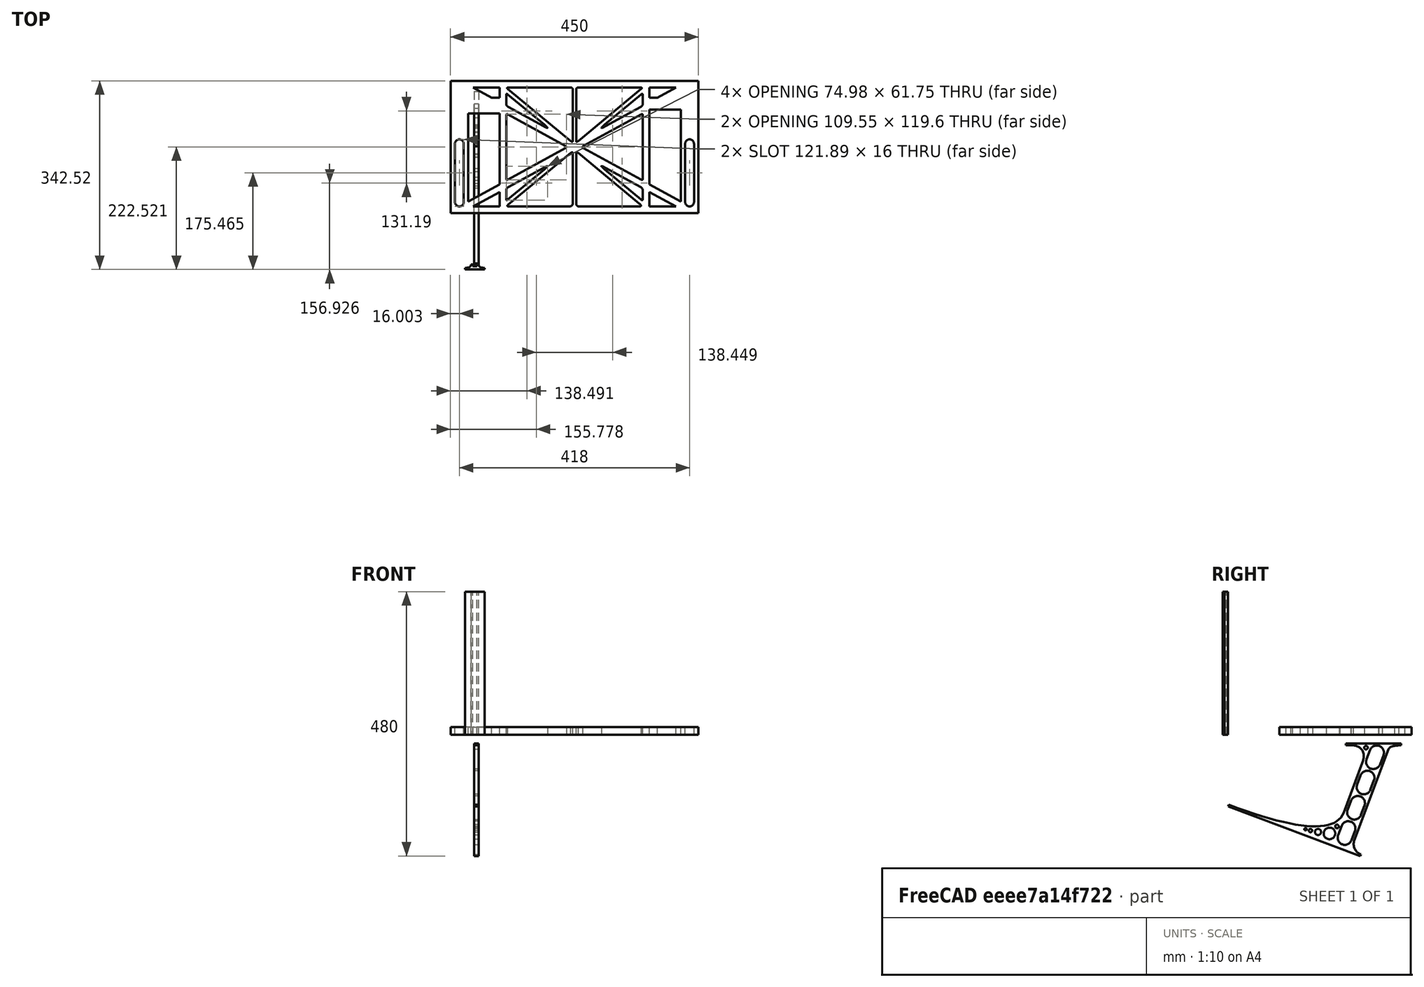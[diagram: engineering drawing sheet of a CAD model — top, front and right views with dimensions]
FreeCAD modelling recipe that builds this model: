
FCSTD DOCUMENT  (FreeCAD 0.19R0.19.2)
Label: laptopStand092
License: All rights reserved
LicenseURL: http://en.wikipedia.org/wiki/All_rights_reserved
objects: Sketcher::SketchObject×3, Part::Extrusion×3
note: 6 computed .brp shape members not serialized (recipe doc carries the construction recipe); baked Part::Feature solids carry a one-line shape summary decoded from their .brp

FEATURE [Sketcher::SketchObject] Sketch
  FullyConstrained = false
  sketch-geometry (251):
    g0: LineSegment StartX=-10.9272 StartY=-82.7794 StartZ=0 EndX=46.0728 EndY=-51.4823 EndZ=0
    g1: LineSegment StartX=366.073 StartY=-91.7794 StartZ=0 EndX=318.073 EndY=-65.424 EndZ=0
    g2: LineSegment StartX=-10.9272 StartY=77.3346 StartZ=0 EndX=-10.9272 EndY=-82.7794 EndZ=0
    g3: LineSegment StartX=375.073 StartY=-82.7794 StartZ=0 EndX=375.073 EndY=83.9235 EndZ=0
    g4: LineSegment StartX=-1.92719 StartY=-91.7794 StartZ=0 EndX=46.0728 EndY=-91.7794 EndZ=0
    g5: LineSegment StartX=318.073 StartY=124.221 StartZ=0 EndX=366.073 EndY=124.221 EndZ=0
    g6: LineSegment StartX=318.073 StartY=83.9235 StartZ=0 EndX=318.073 EndY=-51.4823 EndZ=0
    g7: LineSegment StartX=318.073 StartY=-51.4823 StartZ=0 EndX=375.073 EndY=-82.7794 EndZ=0
    g8: LineSegment StartX=318.073 StartY=-65.424 StartZ=0 EndX=318.073 EndY=-91.7794 EndZ=0
    g9: LineSegment StartX=318.073 StartY=-91.7794 StartZ=0 EndX=366.073 EndY=-91.7794 EndZ=0
    g10: LineSegment StartX=46.0728 StartY=-65.424 StartZ=0 EndX=-1.92719 EndY=-91.7794 EndZ=0
    g11: LineSegment StartX=46.0728 StartY=-65.424 StartZ=0 EndX=46.0728 EndY=-91.7794 EndZ=0
    g12: LineSegment StartX=46.0728 StartY=77.3346 StartZ=0 EndX=46.0728 EndY=-51.4823 EndZ=0
    g13: LineSegment StartX=-42.9272 StartY=136.221 StartZ=0 EndX=-42.9272 EndY=-103.779 EndZ=0
    g14: LineSegment StartX=407.073 StartY=136.221 StartZ=0 EndX=407.073 EndY=-103.779 EndZ=0
    g15: ArcOfCircle CenterX=-26.9272 CenterY=22.1087 CenterZ=0 NormalX=0 NormalY=0 NormalZ=1 AngleXU=0 Radius=8 StartAngle=1e-16 EndAngle=3.14159
    g16: ArcOfCircle CenterX=-26.9272 CenterY=-83.7794 CenterZ=0 NormalX=0 NormalY=0 NormalZ=1 AngleXU=0 Radius=8 StartAngle=3.14159 EndAngle=6.28319
    g17: LineSegment StartX=-34.9272 StartY=22.1087 StartZ=0 EndX=-34.9272 EndY=-83.7794 EndZ=0
    g18: LineSegment StartX=-18.9272 StartY=22.1087 StartZ=0 EndX=-18.9272 EndY=-83.7794 EndZ=0
    g19: ArcOfCircle CenterX=391.073 CenterY=22.1087 CenterZ=0 NormalX=0 NormalY=0 NormalZ=1 AngleXU=0 Radius=8 StartAngle=-4.4e-15 EndAngle=3.14159
    g20: LineSegment StartX=399.073 StartY=22.1087 StartZ=0 EndX=399.073 EndY=-83.7794 EndZ=0
    g21: LineSegment StartX=383.073 StartY=22.1087 StartZ=0 EndX=383.073 EndY=-83.7794 EndZ=0
    g22: ArcOfCircle CenterX=391.073 CenterY=-83.7794 CenterZ=0 NormalX=0 NormalY=0 NormalZ=1 AngleXU=0 Radius=8 StartAngle=3.14159 EndAngle=6.28319
    g23: Circle CenterX=175.022 CenterY=27.0628 CenterZ=0 NormalX=0 NormalY=0 NormalZ=1 AngleXU=0 Radius=1
    g24: Circle CenterX=179.022 CenterY=24.8665 CenterZ=0 NormalX=0 NormalY=0 NormalZ=1 AngleXU=0 Radius=1
    g25: Circle CenterX=179.022 CenterY=27.0628 CenterZ=0 NormalX=0 NormalY=0 NormalZ=1 AngleXU=0 Radius=1
    g26: BSplineCurve PolesCount=3 KnotsCount=2 Degree=2 IsPeriodic=0
    g27: GeomPoint X=175.022 Y=27.0628 Z=0
    g28: GeomPoint X=179.022 Y=27.0628 Z=0
    g29: Circle CenterX=189.124 CenterY=27.0628 CenterZ=0 NormalX=0 NormalY=0 NormalZ=1 AngleXU=0 Radius=1
    g30: Circle CenterX=185.124 CenterY=24.8665 CenterZ=0 NormalX=0 NormalY=0 NormalZ=1 AngleXU=0 Radius=1
    g31: Circle CenterX=185.124 CenterY=27.0628 CenterZ=0 NormalX=0 NormalY=0 NormalZ=1 AngleXU=0 Radius=1
    g32: BSplineCurve PolesCount=3 KnotsCount=2 Degree=2 IsPeriodic=0
    g33: GeomPoint X=189.124 Y=27.0628 Z=0
    g34: GeomPoint X=185.124 Y=27.0628 Z=0
    g35: Circle CenterX=175.022 CenterY=5.37834 CenterZ=0 NormalX=0 NormalY=0 NormalZ=1 AngleXU=0 Radius=1
    g36: Circle CenterX=179.022 CenterY=7.57463 CenterZ=0 NormalX=0 NormalY=0 NormalZ=1 AngleXU=0 Radius=1
    g37: Circle CenterX=179.022 CenterY=5.34704 CenterZ=0 NormalX=0 NormalY=0 NormalZ=1 AngleXU=0 Radius=1
    g38: BSplineCurve PolesCount=3 KnotsCount=2 Degree=2 IsPeriodic=0
    g39: GeomPoint X=175.022 Y=5.37834 Z=0
    g40: GeomPoint X=179.022 Y=5.34704 Z=0
    g41: Circle CenterX=189.124 CenterY=5.37834 CenterZ=0 NormalX=0 NormalY=0 NormalZ=1 AngleXU=0 Radius=1
    g42: Circle CenterX=185.124 CenterY=7.57463 CenterZ=0 NormalX=0 NormalY=0 NormalZ=1 AngleXU=0 Radius=1
    g43: Circle CenterX=185.124 CenterY=5.34704 CenterZ=0 NormalX=0 NormalY=0 NormalZ=1 AngleXU=0 Radius=1
    g44: BSplineCurve PolesCount=3 KnotsCount=2 Degree=2 IsPeriodic=0
    g45: GeomPoint X=189.124 Y=5.37834 Z=0
    g46: GeomPoint X=185.124 Y=5.34704 Z=0
    g47: Circle CenterX=165.871 CenterY=18.1458 CenterZ=0 NormalX=0 NormalY=0 NormalZ=1 AngleXU=0 Radius=1
    g48: Circle CenterX=169.377 CenterY=16.2206 CenterZ=0 NormalX=0 NormalY=0 NormalZ=1 AngleXU=0 Radius=1
    g49: Circle CenterX=165.871 CenterY=14.2954 CenterZ=0 NormalX=0 NormalY=0 NormalZ=1 AngleXU=0 Radius=1
    g50: BSplineCurve PolesCount=3 KnotsCount=2 Degree=2 IsPeriodic=0
    g51: GeomPoint X=165.871 Y=18.1458 Z=0
    g52: GeomPoint X=165.871 Y=14.2954 Z=0
    g53: Circle CenterX=198.275 CenterY=18.1458 CenterZ=0 NormalX=0 NormalY=0 NormalZ=1 AngleXU=0 Radius=1
    g54: Circle CenterX=194.768 CenterY=16.2206 CenterZ=0 NormalX=0 NormalY=0 NormalZ=1 AngleXU=0 Radius=1
    g55: Circle CenterX=198.275 CenterY=14.2954 CenterZ=0 NormalX=0 NormalY=0 NormalZ=1 AngleXU=0 Radius=1
    g56: BSplineCurve PolesCount=3 KnotsCount=2 Degree=2 IsPeriodic=0
    g57: GeomPoint X=198.275 Y=18.1458 Z=0
    g58: GeomPoint X=198.275 Y=14.2954 Z=0
    g59: LineSegment StartX=407.073 StartY=-103.779 StartZ=0 EndX=-42.9272 EndY=-103.779 EndZ=0
    g60: LineSegment StartX=407.073 StartY=136.221 StartZ=0 EndX=-42.9272 EndY=136.221 EndZ=0
    g61: LineSegment StartX=46.0728 StartY=77.3346 StartZ=0 EndX=-10.9272 EndY=77.3346 EndZ=0
    g62: LineSegment StartX=46.0728 StartY=105.865 StartZ=0 EndX=31.5028 EndY=105.865 EndZ=0
    g63: LineSegment StartX=46.0728 StartY=124.221 StartZ=0 EndX=46.0728 EndY=105.865 EndZ=0
    g64: LineSegment StartX=-1.92719 StartY=124.221 StartZ=0 EndX=31.5028 EndY=105.865 EndZ=0
    g65: LineSegment StartX=46.0728 StartY=124.221 StartZ=0 EndX=-1.92719 EndY=124.221 EndZ=0
    g66: LineSegment StartX=318.073 StartY=83.9235 StartZ=0 EndX=375.073 EndY=83.9235 EndZ=0
    g67: LineSegment StartX=318.073 StartY=105.865 StartZ=0 EndX=332.643 EndY=105.865 EndZ=0
    g68: LineSegment StartX=332.643 StartY=105.865 StartZ=0 EndX=366.073 EndY=124.221 EndZ=0
    g69: LineSegment StartX=318.073 StartY=124.221 StartZ=0 EndX=318.073 EndY=105.865 EndZ=0
    g70: Circle CenterX=125.607 CenterY=54.1951 CenterZ=0 NormalX=0 NormalY=0 NormalZ=1 AngleXU=0 Radius=1
    g71: Circle CenterX=139.632 CenterY=46.4944 CenterZ=0 NormalX=0 NormalY=0 NormalZ=1 AngleXU=0 Radius=1
    g72: Circle CenterX=127.326 CenterY=56.7187 CenterZ=0 NormalX=0 NormalY=0 NormalZ=1 AngleXU=0 Radius=1
    g73: BSplineCurve PolesCount=3 KnotsCount=2 Degree=2 IsPeriodic=0
    g74: GeomPoint X=125.607 Y=54.1951 Z=0
    g75: GeomPoint X=127.326 Y=56.7187 Z=0
    g76: Circle CenterX=236.821 CenterY=56.7187 CenterZ=0 NormalX=0 NormalY=0 NormalZ=1 AngleXU=0 Radius=1
    g77: Circle CenterX=224.513 CenterY=46.4944 CenterZ=0 NormalX=0 NormalY=0 NormalZ=1 AngleXU=0 Radius=1
    g78: Circle CenterX=238.538 CenterY=54.1951 CenterZ=0 NormalX=0 NormalY=0 NormalZ=1 AngleXU=0 Radius=1
    g79: BSplineCurve PolesCount=3 KnotsCount=2 Degree=2 IsPeriodic=0
    g80: GeomPoint X=236.821 Y=56.7187 Z=0
    g81: GeomPoint X=238.538 Y=54.1951 Z=0
    g82: Circle CenterX=238.538 CenterY=-21.7539 CenterZ=0 NormalX=0 NormalY=0 NormalZ=1 AngleXU=0 Radius=1
    g83: Circle CenterX=224.513 CenterY=-14.0532 CenterZ=0 NormalX=0 NormalY=0 NormalZ=1 AngleXU=0 Radius=1
    g84: Circle CenterX=236.821 CenterY=-24.2775 CenterZ=0 NormalX=0 NormalY=0 NormalZ=1 AngleXU=0 Radius=1
    g85: BSplineCurve PolesCount=3 KnotsCount=2 Degree=2 IsPeriodic=0
    g86: GeomPoint X=238.538 Y=-21.7539 Z=0
    g87: GeomPoint X=236.821 Y=-24.2775 Z=0
    g88: Circle CenterX=125.607 CenterY=-21.7539 CenterZ=0 NormalX=0 NormalY=0 NormalZ=1 AngleXU=0 Radius=1
    g89: Circle CenterX=139.632 CenterY=-14.0532 CenterZ=0 NormalX=0 NormalY=0 NormalZ=1 AngleXU=0 Radius=1
    g90: Circle CenterX=127.325 CenterY=-24.2775 CenterZ=0 NormalX=0 NormalY=0 NormalZ=1 AngleXU=0 Radius=1
    g91: BSplineCurve PolesCount=3 KnotsCount=2 Degree=2 IsPeriodic=0
    g92: GeomPoint X=125.607 Y=-21.7539 Z=0
    g93: GeomPoint X=127.325 Y=-24.2775 Z=0
    g94: Circle CenterX=302.996 CenterY=111.695 CenterZ=0 NormalX=0 NormalY=0 NormalZ=1 AngleXU=0 Radius=1
    g95: Circle CenterX=306.073 CenterY=114.251 CenterZ=0 NormalX=0 NormalY=0 NormalZ=1 AngleXU=0 Radius=1
    g96: Circle CenterX=306.073 CenterY=110.251 CenterZ=0 NormalX=0 NormalY=0 NormalZ=1 AngleXU=0 Radius=1
    g97: BSplineCurve PolesCount=3 KnotsCount=2 Degree=2 IsPeriodic=0
    g98: GeomPoint X=302.996 Y=111.695 Z=0
    g99: GeomPoint X=306.073 Y=110.251 Z=0
    g100: Circle CenterX=306.073 CenterY=95.2763 CenterZ=0 NormalX=0 NormalY=0 NormalZ=1 AngleXU=0 Radius=1
    g101: Circle CenterX=306.073 CenterY=91.2763 CenterZ=0 NormalX=0 NormalY=0 NormalZ=1 AngleXU=0 Radius=1
    g102: Circle CenterX=302.567 CenterY=89.3511 CenterZ=0 NormalX=0 NormalY=0 NormalZ=1 AngleXU=0 Radius=1
    g103: BSplineCurve PolesCount=3 KnotsCount=2 Degree=2 IsPeriodic=0
    g104: GeomPoint X=306.073 Y=95.2763 Z=0
    g105: GeomPoint X=302.567 Y=89.3511 Z=0
    g106: LineSegment StartX=306.073 StartY=110.251 StartZ=0 EndX=306.073 EndY=95.2763 EndZ=0
    g107: LineSegment StartX=302.996 StartY=111.695 StartZ=0 EndX=236.821 EndY=56.7187 EndZ=0
    g108: LineSegment StartX=238.538 StartY=54.1951 StartZ=0 EndX=302.567 EndY=89.3511 EndZ=0
    g109: Circle CenterX=61.1496 CenterY=111.695 CenterZ=0 NormalX=0 NormalY=0 NormalZ=1 AngleXU=0 Radius=1
    g110: Circle CenterX=58.0728 CenterY=114.251 CenterZ=0 NormalX=0 NormalY=0 NormalZ=1 AngleXU=0 Radius=1
    g111: Circle CenterX=58.0728 CenterY=110.251 CenterZ=0 NormalX=0 NormalY=0 NormalZ=1 AngleXU=0 Radius=1
    g112: BSplineCurve PolesCount=3 KnotsCount=2 Degree=2 IsPeriodic=0
    g113: GeomPoint X=61.1496 Y=111.695 Z=0
    g114: GeomPoint X=58.0728 Y=110.251 Z=0
    g115: Circle CenterX=61.5791 CenterY=89.3511 CenterZ=0 NormalX=0 NormalY=0 NormalZ=1 AngleXU=0 Radius=1
    g116: Circle CenterX=58.0728 CenterY=91.2763 CenterZ=0 NormalX=0 NormalY=0 NormalZ=1 AngleXU=0 Radius=1
    g117: Circle CenterX=58.0728 CenterY=95.2763 CenterZ=0 NormalX=0 NormalY=0 NormalZ=1 AngleXU=0 Radius=1
    g118: BSplineCurve PolesCount=3 KnotsCount=2 Degree=2 IsPeriodic=0
    g119: GeomPoint X=61.5791 Y=89.3511 Z=0
    g120: GeomPoint X=58.0728 Y=95.2763 Z=0
    g121: LineSegment StartX=58.0728 StartY=110.251 StartZ=0 EndX=58.0728 EndY=95.2763 EndZ=0
    g122: LineSegment StartX=61.1496 StartY=111.695 StartZ=0 EndX=127.326 EndY=56.7187 EndZ=0
    g123: LineSegment StartX=125.607 StartY=54.1951 StartZ=0 EndX=61.5791 EndY=89.3511 EndZ=0
    g124: Circle CenterX=61.5791 CenterY=-56.9099 CenterZ=0 NormalX=0 NormalY=0 NormalZ=1 AngleXU=0 Radius=1
    g125: Circle CenterX=58.0728 CenterY=-58.8351 CenterZ=0 NormalX=0 NormalY=0 NormalZ=1 AngleXU=0 Radius=1
    g126: Circle CenterX=58.0728 CenterY=-62.8351 CenterZ=0 NormalX=0 NormalY=0 NormalZ=1 AngleXU=0 Radius=1
    g127: BSplineCurve PolesCount=3 KnotsCount=2 Degree=2 IsPeriodic=0
    g128: GeomPoint X=61.5791 Y=-56.9099 Z=0
    g129: GeomPoint X=58.0728 Y=-62.8351 Z=0
    g130: Circle CenterX=58.0728 CenterY=-77.8102 CenterZ=0 NormalX=0 NormalY=0 NormalZ=1 AngleXU=0 Radius=1
    g131: Circle CenterX=58.0728 CenterY=-81.8102 CenterZ=0 NormalX=0 NormalY=0 NormalZ=1 AngleXU=0 Radius=1
    g132: Circle CenterX=61.1496 CenterY=-79.2541 CenterZ=0 NormalX=0 NormalY=0 NormalZ=1 AngleXU=0 Radius=1
    g133: BSplineCurve PolesCount=3 KnotsCount=2 Degree=2 IsPeriodic=0
    g134: GeomPoint X=58.0728 Y=-77.8102 Z=0
    g135: GeomPoint X=61.1496 Y=-79.2541 Z=0
    g136: LineSegment StartX=58.0728 StartY=-62.8351 StartZ=0 EndX=58.0728 EndY=-77.8102 EndZ=0
    g137: LineSegment StartX=61.1496 StartY=-79.2541 StartZ=0 EndX=127.325 EndY=-24.2775 EndZ=0
    g138: LineSegment StartX=125.607 StartY=-21.7539 StartZ=0 EndX=61.5791 EndY=-56.9099 EndZ=0
    g139: Circle CenterX=302.567 CenterY=-56.9099 CenterZ=0 NormalX=0 NormalY=0 NormalZ=1 AngleXU=0 Radius=1
    g140: Circle CenterX=306.073 CenterY=-58.8351 CenterZ=0 NormalX=0 NormalY=0 NormalZ=1 AngleXU=0 Radius=1
    g141: Circle CenterX=306.073 CenterY=-62.8351 CenterZ=0 NormalX=0 NormalY=0 NormalZ=1 AngleXU=0 Radius=1
    g142: BSplineCurve PolesCount=3 KnotsCount=2 Degree=2 IsPeriodic=0
    g143: GeomPoint X=302.567 Y=-56.9099 Z=0
    g144: GeomPoint X=306.073 Y=-62.8351 Z=0
    g145: Circle CenterX=302.996 CenterY=-79.2541 CenterZ=0 NormalX=0 NormalY=0 NormalZ=1 AngleXU=0 Radius=1
    g146: Circle CenterX=306.073 CenterY=-81.8102 CenterZ=0 NormalX=0 NormalY=0 NormalZ=1 AngleXU=0 Radius=1
    g147: Circle CenterX=306.073 CenterY=-77.8102 CenterZ=0 NormalX=0 NormalY=0 NormalZ=1 AngleXU=0 Radius=1
    g148: BSplineCurve PolesCount=3 KnotsCount=2 Degree=2 IsPeriodic=0
    g149: GeomPoint X=302.996 Y=-79.2541 Z=0
    g150: GeomPoint X=306.073 Y=-77.8102 Z=0
    g151: LineSegment StartX=306.073 StartY=-62.8351 StartZ=0 EndX=306.073 EndY=-77.8102 EndZ=0
    g152: LineSegment StartX=302.996 StartY=-79.2541 StartZ=0 EndX=236.821 EndY=-24.2775 EndZ=0
    g153: LineSegment StartX=238.538 StartY=-21.7539 StartZ=0 EndX=302.567 EndY=-56.9099 EndZ=0
    g154: Circle CenterX=61.6457 CenterY=-88.8112 CenterZ=0 NormalX=0 NormalY=0 NormalZ=1 AngleXU=0 Radius=1
    g155: Circle CenterX=58.0728 CenterY=-91.7794 CenterZ=0 NormalX=0 NormalY=0 NormalZ=1 AngleXU=0 Radius=1
    g156: Circle CenterX=63.9135 CenterY=-91.7794 CenterZ=0 NormalX=0 NormalY=0 NormalZ=1 AngleXU=0 Radius=1
    g157: BSplineCurve PolesCount=3 KnotsCount=2 Degree=2 IsPeriodic=0
    g158: GeomPoint X=61.6457 Y=-88.8112 Z=0
    g159: GeomPoint X=63.9135 Y=-91.7794 Z=0
    g160: Circle CenterX=179.022 CenterY=-85.8163 CenterZ=0 NormalX=0 NormalY=0 NormalZ=1 AngleXU=0 Radius=1
    g161: Circle CenterX=179.022 CenterY=-91.7794 CenterZ=0 NormalX=0 NormalY=0 NormalZ=1 AngleXU=0 Radius=1
    g162: Circle CenterX=171.895 CenterY=-91.7794 CenterZ=0 NormalX=0 NormalY=0 NormalZ=1 AngleXU=0 Radius=1
    g163: BSplineCurve PolesCount=3 KnotsCount=2 Degree=2 IsPeriodic=0
    g164: GeomPoint X=179.022 Y=-85.8163 Z=0
    g165: GeomPoint X=171.895 Y=-91.7794 Z=0
    g166: Circle CenterX=185.124 CenterY=-86.2028 CenterZ=0 NormalX=0 NormalY=0 NormalZ=1 AngleXU=0 Radius=1
    g167: Circle CenterX=185.124 CenterY=-91.7794 CenterZ=0 NormalX=0 NormalY=0 NormalZ=1 AngleXU=0 Radius=1
    g168: Circle CenterX=191.747 CenterY=-91.7794 CenterZ=0 NormalX=0 NormalY=0 NormalZ=1 AngleXU=0 Radius=1
    g169: BSplineCurve PolesCount=3 KnotsCount=2 Degree=2 IsPeriodic=0
    g170: GeomPoint X=185.124 Y=-86.2028 Z=0
    g171: GeomPoint X=191.747 Y=-91.7794 Z=0
    g172: Circle CenterX=299.888 CenterY=-86.6413 CenterZ=0 NormalX=0 NormalY=0 NormalZ=1 AngleXU=0 Radius=1
    g173: Circle CenterX=306.073 CenterY=-91.7794 CenterZ=0 NormalX=0 NormalY=0 NormalZ=1 AngleXU=0 Radius=1
    g174: Circle CenterX=298.776 CenterY=-91.7794 CenterZ=0 NormalX=0 NormalY=0 NormalZ=1 AngleXU=0 Radius=1
    g175: BSplineCurve PolesCount=3 KnotsCount=2 Degree=2 IsPeriodic=0
    g176: GeomPoint X=299.888 Y=-86.6413 Z=0
    g177: GeomPoint X=298.776 Y=-91.7794 Z=0
    g178: LineSegment StartX=189.124 StartY=5.37834 StartZ=0 EndX=299.888 EndY=-86.6413 EndZ=0
    g179: LineSegment StartX=298.776 StartY=-91.7794 StartZ=0 EndX=191.747 EndY=-91.7794 EndZ=0
    g180: LineSegment StartX=185.124 StartY=-86.2028 StartZ=0 EndX=185.124 EndY=5.34704 EndZ=0
    g181: LineSegment StartX=179.022 StartY=5.34704 StartZ=0 EndX=179.022 EndY=-85.8163 EndZ=0
    g182: LineSegment StartX=171.895 StartY=-91.7794 StartZ=0 EndX=63.9135 EndY=-91.7794 EndZ=0
    g183: LineSegment StartX=61.6457 StartY=-88.8112 StartZ=0 EndX=175.022 EndY=5.37834 EndZ=0
    g184: Circle CenterX=302.073 CenterY=124.221 CenterZ=0 NormalX=0 NormalY=0 NormalZ=1 AngleXU=0 Radius=1
    g185: Circle CenterX=306.073 CenterY=124.221 CenterZ=0 NormalX=0 NormalY=0 NormalZ=1 AngleXU=0 Radius=1
    g186: Circle CenterX=302.996 CenterY=121.665 CenterZ=0 NormalX=0 NormalY=0 NormalZ=1 AngleXU=0 Radius=1
    g187: BSplineCurve PolesCount=3 KnotsCount=2 Degree=2 IsPeriodic=0
    g188: GeomPoint X=302.073 Y=124.221 Z=0
    g189: GeomPoint X=302.996 Y=121.665 Z=0
    g190: Circle CenterX=189.124 CenterY=124.221 CenterZ=0 NormalX=0 NormalY=0 NormalZ=1 AngleXU=0 Radius=1
    g191: Circle CenterX=185.124 CenterY=124.221 CenterZ=0 NormalX=0 NormalY=0 NormalZ=1 AngleXU=0 Radius=1
    g192: Circle CenterX=185.124 CenterY=120.221 CenterZ=0 NormalX=0 NormalY=0 NormalZ=1 AngleXU=0 Radius=1
    g193: BSplineCurve PolesCount=3 KnotsCount=2 Degree=2 IsPeriodic=0
    g194: GeomPoint X=189.124 Y=124.221 Z=0
    g195: GeomPoint X=185.124 Y=120.221 Z=0
    g196: Circle CenterX=175.022 CenterY=124.221 CenterZ=0 NormalX=0 NormalY=0 NormalZ=1 AngleXU=0 Radius=1
    g197: Circle CenterX=179.022 CenterY=124.221 CenterZ=0 NormalX=0 NormalY=0 NormalZ=1 AngleXU=0 Radius=1
    g198: Circle CenterX=179.022 CenterY=120.221 CenterZ=0 NormalX=0 NormalY=0 NormalZ=1 AngleXU=0 Radius=1
    g199: BSplineCurve PolesCount=3 KnotsCount=2 Degree=2 IsPeriodic=0
    g200: GeomPoint X=175.022 Y=124.221 Z=0
    g201: GeomPoint X=179.022 Y=120.221 Z=0
    g202: Circle CenterX=62.0728 CenterY=124.221 CenterZ=0 NormalX=0 NormalY=0 NormalZ=1 AngleXU=0 Radius=1
    g203: Circle CenterX=58.0728 CenterY=124.221 CenterZ=0 NormalX=0 NormalY=0 NormalZ=1 AngleXU=0 Radius=1
    g204: Circle CenterX=61.1496 CenterY=121.665 CenterZ=0 NormalX=0 NormalY=0 NormalZ=1 AngleXU=0 Radius=1
    g205: BSplineCurve PolesCount=3 KnotsCount=2 Degree=2 IsPeriodic=0
    g206: GeomPoint X=62.0728 Y=124.221 Z=0
    g207: GeomPoint X=61.1496 Y=121.665 Z=0
    g208: LineSegment StartX=62.0728 StartY=124.221 StartZ=0 EndX=175.022 EndY=124.221 EndZ=0
    g209: LineSegment StartX=179.022 StartY=120.221 StartZ=0 EndX=179.022 EndY=27.0628 EndZ=0
    g210: LineSegment StartX=185.124 StartY=27.0628 StartZ=0 EndX=185.124 EndY=120.221 EndZ=0
    g211: LineSegment StartX=189.124 StartY=124.221 StartZ=0 EndX=302.073 EndY=124.221 EndZ=0
    g212: LineSegment StartX=302.996 StartY=121.665 StartZ=0 EndX=189.124 EndY=27.0628 EndZ=0
    g213: LineSegment StartX=175.022 StartY=27.0628 StartZ=0 EndX=61.1496 EndY=121.665 EndZ=0
    g214: Circle CenterX=61.5791 CenterY=75.4095 CenterZ=0 NormalX=0 NormalY=0 NormalZ=1 AngleXU=0 Radius=1
    g215: Circle CenterX=58.0728 CenterY=77.3346 CenterZ=0 NormalX=0 NormalY=0 NormalZ=1 AngleXU=0 Radius=1
    g216: Circle CenterX=58.0728 CenterY=73.3346 CenterZ=0 NormalX=0 NormalY=0 NormalZ=1 AngleXU=0 Radius=1
    g217: BSplineCurve PolesCount=3 KnotsCount=2 Degree=2 IsPeriodic=0
    g218: GeomPoint X=61.5791 Y=75.4095 Z=0
    g219: GeomPoint X=58.0728 Y=73.3346 Z=0
    g220: Circle CenterX=58.0728 CenterY=-40.8935 CenterZ=0 NormalX=0 NormalY=0 NormalZ=1 AngleXU=0 Radius=1
    g221: Circle CenterX=58.0728 CenterY=-44.8935 CenterZ=0 NormalX=0 NormalY=0 NormalZ=1 AngleXU=0 Radius=1
    g222: Circle CenterX=61.5791 CenterY=-42.9683 CenterZ=0 NormalX=0 NormalY=0 NormalZ=1 AngleXU=0 Radius=1
    g223: BSplineCurve PolesCount=3 KnotsCount=2 Degree=2 IsPeriodic=0
    g224: GeomPoint X=58.0728 Y=-40.8935 Z=0
    g225: GeomPoint X=61.5791 Y=-42.9683 Z=0
    g226: LineSegment StartX=61.5791 StartY=-42.9683 StartZ=0 EndX=165.871 EndY=14.2954 EndZ=0
    g227: LineSegment StartX=165.871 StartY=18.1458 StartZ=0 EndX=61.5791 EndY=75.4095 EndZ=0
    g228: LineSegment StartX=58.0728 StartY=73.3346 StartZ=0 EndX=58.0728 EndY=-40.8935 EndZ=0
    g229: Circle CenterX=302.567 CenterY=-42.9683 CenterZ=0 NormalX=0 NormalY=0 NormalZ=1 AngleXU=0 Radius=1
    g230: Circle CenterX=306.073 CenterY=-44.8935 CenterZ=0 NormalX=0 NormalY=0 NormalZ=1 AngleXU=0 Radius=1
    g231: Circle CenterX=306.073 CenterY=-40.8935 CenterZ=0 NormalX=0 NormalY=0 NormalZ=1 AngleXU=0 Radius=1
    g232: BSplineCurve PolesCount=3 KnotsCount=2 Degree=2 IsPeriodic=0
    g233: GeomPoint X=302.567 Y=-42.9683 Z=0
    g234: GeomPoint X=306.073 Y=-40.8935 Z=0
    g235: Circle CenterX=306.073 CenterY=73.3346 CenterZ=0 NormalX=0 NormalY=0 NormalZ=1 AngleXU=0 Radius=1
    g236: Circle CenterX=306.073 CenterY=77.3346 CenterZ=0 NormalX=0 NormalY=0 NormalZ=1 AngleXU=0 Radius=1
    g237: Circle CenterX=302.567 CenterY=75.4095 CenterZ=0 NormalX=0 NormalY=0 NormalZ=1 AngleXU=0 Radius=1
    g238: BSplineCurve PolesCount=3 KnotsCount=2 Degree=2 IsPeriodic=0
    g239: GeomPoint X=306.073 Y=73.3346 Z=0
    g240: GeomPoint X=302.567 Y=75.4095 Z=0
    g241: LineSegment StartX=302.567 StartY=-42.9683 StartZ=0 EndX=198.275 EndY=14.2954 EndZ=0
    g242: LineSegment StartX=198.275 StartY=18.1458 StartZ=0 EndX=302.567 EndY=75.4095 EndZ=0
    g243: LineSegment StartX=306.073 StartY=73.3346 StartZ=0 EndX=306.073 EndY=-40.8935 EndZ=0
    g244: LineSegment StartX=318.742 StartY=125.546 StartZ=0 EndX=324.381 EndY=125.546 EndZ=0
    g245: LineSegment StartX=365.72 StartY=125.086 StartZ=0 EndX=359.563 EndY=125.086 EndZ=0
    g246: LineSegment StartX=328.264 StartY=104.661 StartZ=0 EndX=331.86 EndY=104.661 EndZ=0
    g247: LineSegment StartX=335.6 StartY=105.351 StartZ=0 EndX=339.311 EndY=107.624 EndZ=0
    g248: LineSegment StartX=366.554 StartY=122.928 StartZ=0 EndX=363.62 EndY=120.771 EndZ=0
    g249: LineSegment StartX=317.217 StartY=106.3 StartZ=0 EndX=317.217 EndY=110.702 EndZ=0
    g250: LineSegment StartX=318.656 StartY=104.747 StartZ=0 EndX=322.194 EndY=104.747 EndZ=0
  constraints (420):
    c: Horizontal(g4)
    c: Horizontal(g5)
    c: Coincident(g6,g7)
    c: Coincident(g8,g1)
    c: Tangent(g6,g8)
    c: Coincident(g11,g10)
    c: Coincident(g0,g12)
    c: Block(g7)
    c: Block(g3)
    c: Block(g1)
    c: Block(g8)
    c: Block(g11)
    c: Block(g10)
    c: Block(g0)
    c: Block(g2)
    c: Block(g5)
    c: Block(g9)
    c: Block(g4)
    c: Vertical(g13)
    c: Vertical(g14)
    c: Block(g14)
    c: Block(g13)
    c: Tangent(g15,g18) = 1.5708
    c: Tangent(g15,g17) = -1.5708
    c: Tangent(g17,g16) = -1.5708
    c: Tangent(g18,g16) = 1.5708
    c: Vertical(g17)
    c: Equal(g15,g16)
    c: Block(g18)
    c: Block(g17)
    c: Tangent(g19,g20) = 1.5708
    c: Tangent(g20,g22) = 1.5708
    c: Equal(g19,g22)
    c: Coincident(g21,g19)
    c: Coincident(g21,g22)
    c: Block(g20)
    c: Block(g21)
    c: Weight(g23) = 1
    c: Equal(g23,g24)
    c: Equal(g23,g25)
    c: InternalAlignment(g23,g26)
    c: InternalAlignment(g24,g26)
    c: InternalAlignment(g25,g26)
    c: InternalAlignment(g27,g26)
    c: InternalAlignment(g28,g26)
    c: Weight(g29) = 1
    c: Equal(g29,g30)
    c: Equal(g29,g31)
    c: InternalAlignment(g29,g32)
    c: InternalAlignment(g30,g32)
    c: InternalAlignment(g31,g32)
    c: InternalAlignment(g33,g32)
    c: InternalAlignment(g34,g32)
    c: Block(g32)
    c: Block(g26)
    c: Weight(g35) = 1
    c: Equal(g35,g36)
    c: Equal(g35,g37)
    c: InternalAlignment(g35,g38)
    c: InternalAlignment(g36,g38)
    c: InternalAlignment(g37,g38)
    c: InternalAlignment(g39,g38)
    c: InternalAlignment(g40,g38)
    c: Weight(g41) = 1
    c: Equal(g41,g42)
    c: Equal(g41,g43)
    c: InternalAlignment(g41,g44)
    c: InternalAlignment(g42,g44)
    c: InternalAlignment(g43,g44)
    c: InternalAlignment(g45,g44)
    c: InternalAlignment(g46,g44)
    c: Block(g44)
    c: Block(g38)
    c: Weight(g47) = 1
    c: Equal(g47,g48)
    c: Equal(g47,g49)
    c: InternalAlignment(g47,g50)
    c: InternalAlignment(g48,g50)
    c: InternalAlignment(g49,g50)
    c: InternalAlignment(g51,g50)
    c: InternalAlignment(g52,g50)
    c: Weight(g53) = 1
    c: Equal(g53,g54)
    c: Equal(g53,g55)
    c: InternalAlignment(g53,g56)
    c: InternalAlignment(g54,g56)
    c: InternalAlignment(g55,g56)
    c: InternalAlignment(g57,g56)
    c: InternalAlignment(g58,g56)
    c: Block(g50)
    c: Block(g56)
    c: Coincident(g59,g14)
    c: Coincident(g59,g13)
    c: Horizontal(g59)
    c: Distance(g59) = 450
    c: Coincident(g60,g14)
    c: Coincident(g60,g13)
    c: Horizontal(g60)
    c: Horizontal(g61)
    c: Coincident(g12,g61)
    c: Horizontal(g62)
    c: Vertical(g63)
    c: Block(g63)
    c: Block(g62)
    c: Block(g61)
    c: Distance(g63) = 18.3554
    c: Coincident(g65,g63)
    c: Coincident(g65,g64)
    c: Horizontal(g65)
    c: Block(g65)
    c: Block(g64)
    c: Coincident(g62,g64)
    c: Coincident(g2,g61)
    c: Coincident(g66,g6)
    c: Horizontal(g66)
    c: Horizontal(g67)
    c: Block(g66)
    c: Coincident(g68,g5)
    c: Coincident(g69,g5)
    c: Coincident(g69,g67)
    c: Vertical(g69)
    c: Block(g69)
    c: Coincident(g67,g68)
    c: Block(g68)
    c: Coincident(g3,g66)
    c: Weight(g70) = 1
    c: Equal(g70,g71)
    c: Equal(g70,g72)
    c: InternalAlignment(g70,g73)
    c: InternalAlignment(g71,g73)
    c: InternalAlignment(g72,g73)
    c: InternalAlignment(g74,g73)
    c: InternalAlignment(g75,g73)
    c: Block(g73)
    c: Weight(g76) = 1
    c: Equal(g76,g77)
    c: Equal(g76,g78)
    c: InternalAlignment(g76,g79)
    c: InternalAlignment(g77,g79)
    c: InternalAlignment(g78,g79)
    c: InternalAlignment(g80,g79)
    c: InternalAlignment(g81,g79)
    c: Block(g79)
    c: Weight(g82) = 1
    c: Equal(g82,g83)
    c: Equal(g82,g84)
    c: InternalAlignment(g82,g85)
    c: InternalAlignment(g83,g85)
    c: InternalAlignment(g84,g85)
    c: InternalAlignment(g86,g85)
    c: InternalAlignment(g87,g85)
    c: Block(g85)
    c: Weight(g88) = 1
    c: Equal(g88,g89)
    c: Equal(g88,g90)
    c: InternalAlignment(g88,g91)
    c: InternalAlignment(g89,g91)
    c: InternalAlignment(g90,g91)
    c: InternalAlignment(g92,g91)
    c: InternalAlignment(g93,g91)
    c: Block(g91)
    c: Weight(g94) = 1
    c: Equal(g94,g95)
    c: Equal(g94,g96)
    c: InternalAlignment(g94,g97)
    c: InternalAlignment(g95,g97)
    c: InternalAlignment(g96,g97)
    c: InternalAlignment(g98,g97)
    c: InternalAlignment(g99,g97)
    c: Weight(g100) = 1
    c: Equal(g100,g101)
    c: Equal(g100,g102)
    c: InternalAlignment(g100,g103)
    c: InternalAlignment(g101,g103)
    c: InternalAlignment(g102,g103)
    c: InternalAlignment(g104,g103)
    c: InternalAlignment(g105,g103)
    c: Block(g97)
    c: Block(g103)
    c: Coincident(g106,g97)
    c: Coincident(g106,g103)
    c: Vertical(g106)
    c: Coincident(g107,g97)
    c: Coincident(g107,g79)
    c: Coincident(g108,g79)
    c: Coincident(g108,g103)
    c: Weight(g109) = 1
    c: Equal(g109,g110)
    c: Equal(g109,g111)
    c: InternalAlignment(g109,g112)
    c: InternalAlignment(g110,g112)
    c: InternalAlignment(g111,g112)
    c: InternalAlignment(g113,g112)
    c: InternalAlignment(g114,g112)
    c: Weight(g115) = 1
    c: Equal(g115,g116)
    c: Equal(g115,g117)
    c: InternalAlignment(g115,g118)
    c: InternalAlignment(g116,g118)
    c: InternalAlignment(g117,g118)
    c: InternalAlignment(g119,g118)
    c: InternalAlignment(g120,g118)
    c: Block(g112)
    c: Block(g118)
    c: Coincident(g121,g112)
    c: Coincident(g121,g118)
    c: Vertical(g121)
    c: Coincident(g122,g112)
    c: Coincident(g122,g73)
    c: Coincident(g123,g73)
    c: Coincident(g123,g118)
    c: Weight(g124) = 1
    c: Equal(g124,g125)
    c: Equal(g124,g126)
    c: InternalAlignment(g124,g127)
    c: InternalAlignment(g125,g127)
    c: InternalAlignment(g126,g127)
    c: InternalAlignment(g128,g127)
    c: InternalAlignment(g129,g127)
    c: Weight(g130) = 1
    c: Equal(g130,g131)
    c: Equal(g130,g132)
    c: InternalAlignment(g130,g133)
    c: InternalAlignment(g131,g133)
    c: InternalAlignment(g132,g133)
    c: InternalAlignment(g134,g133)
    c: InternalAlignment(g135,g133)
    c: Block(g127)
    c: Block(g133)
    c: Coincident(g136,g127)
    c: Coincident(g136,g133)
    c: Vertical(g136)
    c: Coincident(g137,g133)
    c: Coincident(g137,g91)
    c: Coincident(g138,g91)
    c: Coincident(g138,g127)
    c: Weight(g139) = 1
    c: Equal(g139,g140)
    c: Equal(g139,g141)
    c: InternalAlignment(g139,g142)
    c: InternalAlignment(g140,g142)
    c: InternalAlignment(g141,g142)
    c: InternalAlignment(g143,g142)
    c: InternalAlignment(g144,g142)
    c: Weight(g145) = 1
    c: Equal(g145,g146)
    c: Equal(g145,g147)
    c: InternalAlignment(g145,g148)
    c: InternalAlignment(g146,g148)
    c: InternalAlignment(g147,g148)
    c: InternalAlignment(g149,g148)
    c: InternalAlignment(g150,g148)
    c: Block(g142)
    c: Block(g148)
    c: Coincident(g151,g142)
    c: Coincident(g151,g148)
    c: Vertical(g151)
    c: Coincident(g152,g148)
    c: Coincident(g152,g85)
    c: Coincident(g153,g85)
    c: Coincident(g153,g142)
    c: Weight(g154) = 1
    c: Equal(g154,g155)
    c: Equal(g154,g156)
    c: InternalAlignment(g154,g157)
    c: InternalAlignment(g155,g157)
    c: InternalAlignment(g156,g157)
    c: InternalAlignment(g158,g157)
    c: InternalAlignment(g159,g157)
    c: Weight(g160) = 1
    c: Equal(g160,g161)
    c: Equal(g160,g162)
    c: InternalAlignment(g160,g163)
    c: InternalAlignment(g161,g163)
    c: InternalAlignment(g162,g163)
    c: InternalAlignment(g164,g163)
    c: InternalAlignment(g165,g163)
    c: Weight(g166) = 1
    c: Equal(g166,g167)
    c: Equal(g166,g168)
    c: InternalAlignment(g166,g169)
    c: InternalAlignment(g167,g169)
    c: InternalAlignment(g168,g169)
    c: InternalAlignment(g170,g169)
    c: InternalAlignment(g171,g169)
    c: Weight(g172) = 1
    c: Equal(g172,g173)
    c: Equal(g172,g174)
    c: InternalAlignment(g172,g175)
    c: InternalAlignment(g173,g175)
    c: InternalAlignment(g174,g175)
    c: InternalAlignment(g176,g175)
    c: InternalAlignment(g177,g175)
    c: Block(g175)
    c: Block(g169)
    c: Block(g163)
    c: Block(g157)
    c: Coincident(g178,g44)
    c: Coincident(g178,g175)
    c: Coincident(g179,g175)
    c: Coincident(g179,g169)
    c: Horizontal(g179)
    c: Coincident(g180,g169)
    c: Coincident(g180,g44)
    c: Vertical(g180)
    c: Coincident(g181,g38)
    c: Coincident(g181,g163)
    c: Vertical(g181)
    c: Coincident(g182,g163)
    c: Coincident(g182,g157)
    c: Horizontal(g182)
    c: Coincident(g183,g157)
    c: Coincident(g183,g38)
    c: Weight(g184) = 1
    c: Equal(g184,g185)
    c: Equal(g184,g186)
    c: InternalAlignment(g184,g187)
    c: InternalAlignment(g185,g187)
    c: InternalAlignment(g186,g187)
    c: InternalAlignment(g188,g187)
    c: InternalAlignment(g189,g187)
    c: Weight(g190) = 1
    c: Equal(g190,g191)
    c: Equal(g190,g192)
    c: InternalAlignment(g190,g193)
    c: InternalAlignment(g191,g193)
    c: InternalAlignment(g192,g193)
    c: InternalAlignment(g194,g193)
    c: InternalAlignment(g195,g193)
    c: Weight(g196) = 1
    c: Equal(g196,g197)
    c: Equal(g196,g198)
    c: InternalAlignment(g196,g199)
    c: InternalAlignment(g197,g199)
    c: InternalAlignment(g198,g199)
    c: InternalAlignment(g200,g199)
    c: InternalAlignment(g201,g199)
    c: Weight(g202) = 1
    c: Equal(g202,g203)
    c: Equal(g202,g204)
    c: InternalAlignment(g202,g205)
    c: InternalAlignment(g203,g205)
    c: InternalAlignment(g204,g205)
    c: InternalAlignment(g206,g205)
    c: InternalAlignment(g207,g205)
    c: Block(g205)
    c: Block(g199)
    c: Block(g193)
    c: Block(g187)
    c: Coincident(g208,g205)
    c: Coincident(g208,g199)
    c: Horizontal(g208)
    c: Coincident(g209,g199)
    c: Coincident(g209,g26)
    c: Vertical(g209)
    c: Coincident(g210,g32)
    c: Coincident(g210,g193)
    c: Vertical(g210)
    c: Coincident(g211,g193)
    c: Coincident(g211,g187)
    c: Horizontal(g211)
    c: Coincident(g212,g187)
    c: Coincident(g212,g32)
    c: Coincident(g213,g26)
    c: Coincident(g213,g205)
    c: Weight(g214) = 1
    c: Equal(g214,g215)
    c: Equal(g214,g216)
    c: InternalAlignment(g214,g217)
    c: InternalAlignment(g215,g217)
    c: InternalAlignment(g216,g217)
    c: InternalAlignment(g218,g217)
    c: InternalAlignment(g219,g217)
    c: Weight(g220) = 1
    c: Equal(g220,g221)
    c: Equal(g220,g222)
    c: InternalAlignment(g220,g223)
    c: InternalAlignment(g221,g223)
    c: InternalAlignment(g222,g223)
    c: InternalAlignment(g224,g223)
    c: InternalAlignment(g225,g223)
    c: Block(g223)
    c: Block(g217)
    c: Coincident(g226,g223)
    c: Coincident(g226,g50)
    c: Coincident(g227,g50)
    c: Coincident(g227,g217)
    c: Coincident(g228,g217)
    c: Coincident(g228,g223)
    c: Vertical(g228)
    c: Weight(g229) = 1
    c: Equal(g229,g230)
    c: Equal(g229,g231)
    c: InternalAlignment(g229,g232)
    c: InternalAlignment(g230,g232)
    c: InternalAlignment(g231,g232)
    c: InternalAlignment(g233,g232)
    c: InternalAlignment(g234,g232)
    c: Weight(g235) = 1
    c: Equal(g235,g236)
    c: Equal(g235,g237)
    c: InternalAlignment(g235,g238)
    c: InternalAlignment(g236,g238)
    c: InternalAlignment(g237,g238)
    c: InternalAlignment(g239,g238)
    c: InternalAlignment(g240,g238)
    c: Block(g238)
    c: Block(g232)
    c: Coincident(g241,g232)
    c: Coincident(g241,g56)
    c: Coincident(g242,g56)
    c: Coincident(g242,g238)
    c: Coincident(g243,g238)
    c: Coincident(g243,g232)
    c: Vertical(g243)
    c: Horizontal(g244)
    c: Horizontal(g245)
    c: Horizontal(g246)
    c: Vertical(g249)
    c: Horizontal(g250)
FEATURE [Sketcher::SketchObject] Sketch001
  FullyConstrained = true
  MapMode = 4
  Placement = pos=(0,0,0) rot=(0.57735,0.57735,0.57735;2.0944rad)
  Support = -> [Sketch]
  sketch-geometry (46):
    g0: BSplineCurve PolesCount=3 KnotsCount=2 Degree=2 IsPeriodic=0
    g1: ArcOfCircle CenterX=73.1223 CenterY=-32.291 CenterZ=0 NormalX=0 NormalY=0 NormalZ=1 AngleXU=0 Radius=13 StartAngle=5.92268 EndAngle=9.06428
    g2: ArcOfCircle CenterX=66.7816 CenterY=-49.1439 CenterZ=0 NormalX=0 NormalY=0 NormalZ=1 AngleXU=0 Radius=13 StartAngle=2.78068 EndAngle=5.92131
    g3: ArcOfCircle CenterX=55.9263 CenterY=-78.1807 CenterZ=0 NormalX=0 NormalY=0 NormalZ=1 AngleXU=0 Radius=13 StartAngle=5.92268 EndAngle=9.06428
    g4: ArcOfCircle CenterX=49.5884 CenterY=-95.0342 CenterZ=0 NormalX=0 NormalY=0 NormalZ=1 AngleXU=0 Radius=13 StartAngle=2.78068 EndAngle=5.92131
    g5: ArcOfCircle CenterX=38.7206 CenterY=-124.067 CenterZ=0 NormalX=0 NormalY=0 NormalZ=1 AngleXU=0 Radius=13 StartAngle=5.92268 EndAngle=9.06428
    g6: ArcOfCircle CenterX=32.3875 CenterY=-140.92 CenterZ=0 NormalX=0 NormalY=0 NormalZ=1 AngleXU=0 Radius=13 StartAngle=2.78068 EndAngle=5.92131
    g7: ArcOfCircle CenterX=21.4715 CenterY=-169.934 CenterZ=0 NormalX=0 NormalY=0 NormalZ=1 AngleXU=0 Radius=13 StartAngle=5.92268 EndAngle=9.06428
    g8: ArcOfCircle CenterX=15.1336 CenterY=-186.787 CenterZ=0 NormalX=0 NormalY=0 NormalZ=1 AngleXU=0 Radius=13 StartAngle=2.78068 EndAngle=5.92131
    g9-g12: Circle x4 (B-spline internal-alignment scaffolding for g13; pole/knot coordinates omitted)
    g13: BSplineCurve PolesCount=4 KnotsCount=2 Degree=3 IsPeriodic=0
    g14: GeomPoint X=28.8094 Y=-19.0875 Z=0
    g15: GeomPoint X=47.0443 Y=-50.4712 Z=0
    g16: Circle CenterX=53.5586 CenterY=-23.2695 CenterZ=0 NormalX=0 NormalY=0 NormalZ=1 AngleXU=0 Radius=3.24518
    g17: Circle CenterX=-195.441 CenterY=-127.082 CenterZ=0 NormalX=0 NormalY=0 NormalZ=1 AngleXU=0 Radius=1
    g18: Circle CenterX=-8.24091 CenterY=-197.481 CenterZ=0 NormalX=0 NormalY=0 NormalZ=1 AngleXU=0 Radius=1
    g19: Circle CenterX=12.8789 CenterY=-141.321 CenterZ=0 NormalX=0 NormalY=0 NormalZ=1 AngleXU=0 Radius=1
    g20: BSplineCurve PolesCount=3 KnotsCount=2 Degree=2 IsPeriodic=0
    g21: GeomPoint X=-195.441 Y=-127.082 Z=0
    g22: GeomPoint X=12.8789 Y=-141.321 Z=0
    g23: Circle CenterX=-12.8016 CenterY=-179.036 CenterZ=0 NormalX=0 NormalY=0 NormalZ=1 AngleXU=0 Radius=10.5072
    g24: Circle CenterX=0.933922 CenterY=-166.43 CenterZ=0 NormalX=0 NormalY=0 NormalZ=1 AngleXU=0 Radius=3.26661
    g25: Circle CenterX=-33.5518 CenterY=-176.44 CenterZ=0 NormalX=0 NormalY=0 NormalZ=1 AngleXU=0 Radius=5.64388
    g26: Circle CenterX=-47.2366 CenterY=-173.859 CenterZ=0 NormalX=0 NormalY=0 NormalZ=1 AngleXU=0 Radius=3.01653
    g27: Circle CenterX=-56.2595 CenterY=-171.456 CenterZ=0 NormalX=0 NormalY=0 NormalZ=1 AngleXU=0 Radius=2.12826
    g28: ArcOfCircle CenterX=51.2151 CenterY=-198.473 CenterZ=0 NormalX=0 NormalY=0 NormalZ=1 AngleXU=0 Radius=20 StartAngle=2.78189 EndAngle=4.35269
    g29: LineSegment StartX=32.4951 StartY=-191.433 StartZ=0 EndX=94.6578 EndY=-26.1352 EndZ=0
    g30: LineSegment StartX=43.1192 StartY=-220.001 StartZ=0 EndX=-196.497 EndY=-129.89 EndZ=0
    g31: LineSegment StartX=43.1192 StartY=-220.001 StartZ=0 EndX=44.1752 EndY=-217.193 EndZ=0
    g32: LineSegment StartX=117.223 StartY=-19.0875 StartZ=0 EndX=117.223 EndY=-16.0875 EndZ=0
    g33: LineSegment StartX=117.223 StartY=-16.0875 StartZ=0 EndX=17.2232 EndY=-16.0875 EndZ=0
    g34: LineSegment StartX=17.2232 StartY=-16.0875 StartZ=0 EndX=17.2232 EndY=-19.0875 EndZ=0
    g35: LineSegment StartX=28.8094 StartY=-19.0875 StartZ=0 EndX=17.2232 EndY=-19.0875 EndZ=0
    g36: LineSegment StartX=47.0443 StartY=-50.4712 StartZ=0 EndX=12.8789 EndY=-141.321 EndZ=0
    g37: LineSegment StartX=-195.441 StartY=-127.082 StartZ=0 EndX=-196.497 EndY=-129.89 EndZ=0
    g38: LineSegment StartX=85.2866 StartY=-36.8766 StartZ=0 EndX=78.9396 EndY=-53.7463 EndZ=0
    g39: LineSegment StartX=60.9579 StartY=-27.7053 StartZ=0 EndX=54.6191 EndY=-44.5532 EndZ=0
    g40: LineSegment StartX=68.0907 StartY=-82.7664 StartZ=0 EndX=61.7465 EndY=-99.6365 EndZ=0
    g41: LineSegment StartX=43.7619 StartY=-73.595 StartZ=0 EndX=37.426 EndY=-90.4435 EndZ=0
    g42: LineSegment StartX=50.885 StartY=-128.652 StartZ=0 EndX=44.5456 EndY=-145.522 EndZ=0
    g43: LineSegment StartX=26.5562 StartY=-119.481 StartZ=0 EndX=20.2251 EndY=-136.329 EndZ=0
    g44: LineSegment StartX=9.3071 StartY=-165.349 StartZ=0 EndX=2.97115 EndY=-182.197 EndZ=0
    g45: LineSegment StartX=33.6358 StartY=-174.52 StartZ=0 EndX=27.2917 EndY=-191.39 EndZ=0
  constraints (71):
    c: Block(g0)
    c: Block(g1)
    c: Block(g2)
    c: Block(g4)
    c: Block(g3)
    c: Block(g6)
    c: Block(g5)
    c: Block(g8)
    c: Block(g7)
    c: Weight(g9) = 1
    c: Equal(g9,g10)
    c: Equal(g9,g11)
    c: Equal(g9,g12)
    c: InternalAlignment(g9-g12 -> g13) x4
    c: InternalAlignment(g14,g13)
    c: InternalAlignment(g15,g13)
    c: Block(g16)
    c: Weight(g17) = 1
    c: Equal(g17,g18)
    c: Equal(g17,g19)
    c: InternalAlignment(g17,g20)
    c: InternalAlignment(g18,g20)
    c: InternalAlignment(g19,g20)
    c: InternalAlignment(g21,g20)
    c: InternalAlignment(g22,g20)
    c: Block(g20)
    c: Block(g23)
    c: Block(g24)
    c: Block(g25)
    c: Block(g26)
    c: Block(g27)
    c: Block(g28)
    c: Coincident(g29,g28)
    c: Coincident(g29,g0)
    c: Block(g13)
    c: Coincident(g31,g30)
    c: Coincident(g31,g28)
    c: Block(g31)
    c: Coincident(g32,g0)
    c: Vertical(g32)
    c: Coincident(g33,g32)
    c: Horizontal(g33)
    c: Coincident(g34,g33)
    c: Vertical(g34)
    c: Block(g33)
    c: Coincident(g35,g13)
    c: Coincident(g35,g34)
    c: Horizontal(g35)
    c: Coincident(g36,g13)
    c: Coincident(g36,g20)
    c: Coincident(g37,g20)
    c: Coincident(g37,g30)
    c: Block(g30)
    c: Coincident(g38,g1)
    c: Coincident(g38,g2)
    c: Coincident(g39,g1)
    c: Coincident(g39,g2)
    c: Coincident(g40,g3)
    c: Coincident(g40,g4)
    c: Coincident(g41,g3)
    c: Coincident(g41,g4)
    c: Coincident(g42,g5)
    c: Coincident(g42,g6)
    c: Coincident(g43,g5)
    c: Coincident(g43,g6)
    c: Coincident(g44,g7)
    c: Coincident(g44,g8)
    c: Coincident(g45,g7)
    c: Coincident(g45,g8)
    c: Distance(g30) = 256
    c: Distance(g33) = 100
FEATURE [Part::Extrusion] Extrude002
  Base = -> Sketch001
  Dir = (1,0,0)
  DirMode = 2
  FaceMakerClass = Part::FaceMakerBullseye
  LengthFwd = 8
  LengthRev = 0
  Solid = true
  Symmetric = false
FEATURE [Sketcher::SketchObject] Sketch002
  FullyConstrained = true
  sketch-geometry (20):
    g0: LineSegment StartX=-2.77179 StartY=-200.304 StartZ=0 EndX=5.22821 EndY=-200.304 EndZ=0
    g1: LineSegment StartX=5.22821 StartY=-200.304 StartZ=0 EndX=5.22821 EndY=-197.304 EndZ=0
    g2: LineSegment StartX=-2.77179 StartY=-200.304 StartZ=0 EndX=-2.77179 EndY=-197.304 EndZ=0
    g3: LineSegment StartX=5.22821 StartY=-197.304 StartZ=0 EndX=8.22821 EndY=-197.304 EndZ=0
    g4: LineSegment StartX=-2.77179 StartY=-197.304 StartZ=0 EndX=-5.77179 EndY=-197.304 EndZ=0
    g5: LineSegment StartX=19.2282 StartY=-203.304 StartZ=0 EndX=19.2282 EndY=-206.304 EndZ=0
    g6: LineSegment StartX=-16.7718 StartY=-203.304 StartZ=0 EndX=-16.7718 EndY=-206.304 EndZ=0
    g7: LineSegment StartX=-16.7718 StartY=-206.304 StartZ=0 EndX=19.2282 EndY=-206.304 EndZ=0
    g8: Circle CenterX=-16.7718 CenterY=-203.304 CenterZ=0 NormalX=0 NormalY=0 NormalZ=1 AngleXU=0 Radius=1
    g9: Circle CenterX=-5.77179 CenterY=-203.304 CenterZ=0 NormalX=0 NormalY=0 NormalZ=1 AngleXU=0 Radius=1
    g10: Circle CenterX=-5.77179 CenterY=-197.304 CenterZ=0 NormalX=0 NormalY=0 NormalZ=1 AngleXU=0 Radius=1
    g11: BSplineCurve PolesCount=3 KnotsCount=2 Degree=2 IsPeriodic=0
    g12: GeomPoint X=-16.7718 Y=-203.304 Z=0
    g13: GeomPoint X=-5.77179 Y=-197.304 Z=0
    g14: Circle CenterX=19.2282 CenterY=-203.304 CenterZ=0 NormalX=0 NormalY=0 NormalZ=1 AngleXU=0 Radius=1
    g15: Circle CenterX=8.22821 CenterY=-203.304 CenterZ=0 NormalX=0 NormalY=0 NormalZ=1 AngleXU=0 Radius=1
    g16: Circle CenterX=8.22821 CenterY=-197.304 CenterZ=0 NormalX=0 NormalY=0 NormalZ=1 AngleXU=0 Radius=1
    g17: BSplineCurve PolesCount=3 KnotsCount=2 Degree=2 IsPeriodic=0
    g18: GeomPoint X=19.2282 Y=-203.304 Z=0
    g19: GeomPoint X=8.22821 Y=-197.304 Z=0
  constraints (41):
    c: Horizontal(g0)
    c: Distance(g0) = 8
    c: Coincident(g1,g0)
    c: Vertical(g1)
    c: Distance(g1) = 3
    c: Coincident(g2,g0)
    c: Vertical(g2)
    c: Distance(g2) = 3
    c: Coincident(g3,g1)
    c: Horizontal(g3)
    c: Distance(g3) = 3
    c: Coincident(g4,g2)
    c: Horizontal(g4)
    c: Distance(g4) = 3
    c: Vertical(g5)
    c: Vertical(g6)
    c: Coincident(g7,g6)
    c: Coincident(g7,g5)
    c: Weight(g8) = 1
    c: Equal(g8,g9)
    c: Equal(g8,g10)
    c: Coincident(g11,g4)
    c: InternalAlignment(g8,g11)
    c: InternalAlignment(g9,g11)
    c: InternalAlignment(g10,g11)
    c: InternalAlignment(g12,g11)
    c: InternalAlignment(g13,g11)
    c: Coincident(g17,g5)
    c: Weight(g14) = 1
    c: Equal(g14,g15)
    c: Equal(g14,g16)
    c: Coincident(g17,g3)
    c: InternalAlignment(g14,g17)
    c: InternalAlignment(g15,g17)
    c: InternalAlignment(g16,g17)
    c: InternalAlignment(g18,g17)
    c: InternalAlignment(g19,g17)
    c: Block(g7)
    c: Block(g17)
    c: Block(g11)
    c: Block(g6)
FEATURE [Part::Extrusion] Extrude003
  Base = -> Sketch002
  Dir = (0,0,1)
  DirMode = 2
  FaceMakerClass = Part::FaceMakerBullseye
  LengthFwd = 260
  LengthRev = 0
  Solid = true
  Symmetric = false
FEATURE [Part::Extrusion] Extrude
  Base = -> Sketch
  Dir = (0,0,1)
  DirMode = 2
  FaceMakerClass = Part::FaceMakerBullseye
  LengthFwd = 14
  LengthRev = 0
  Solid = true
  Symmetric = false
